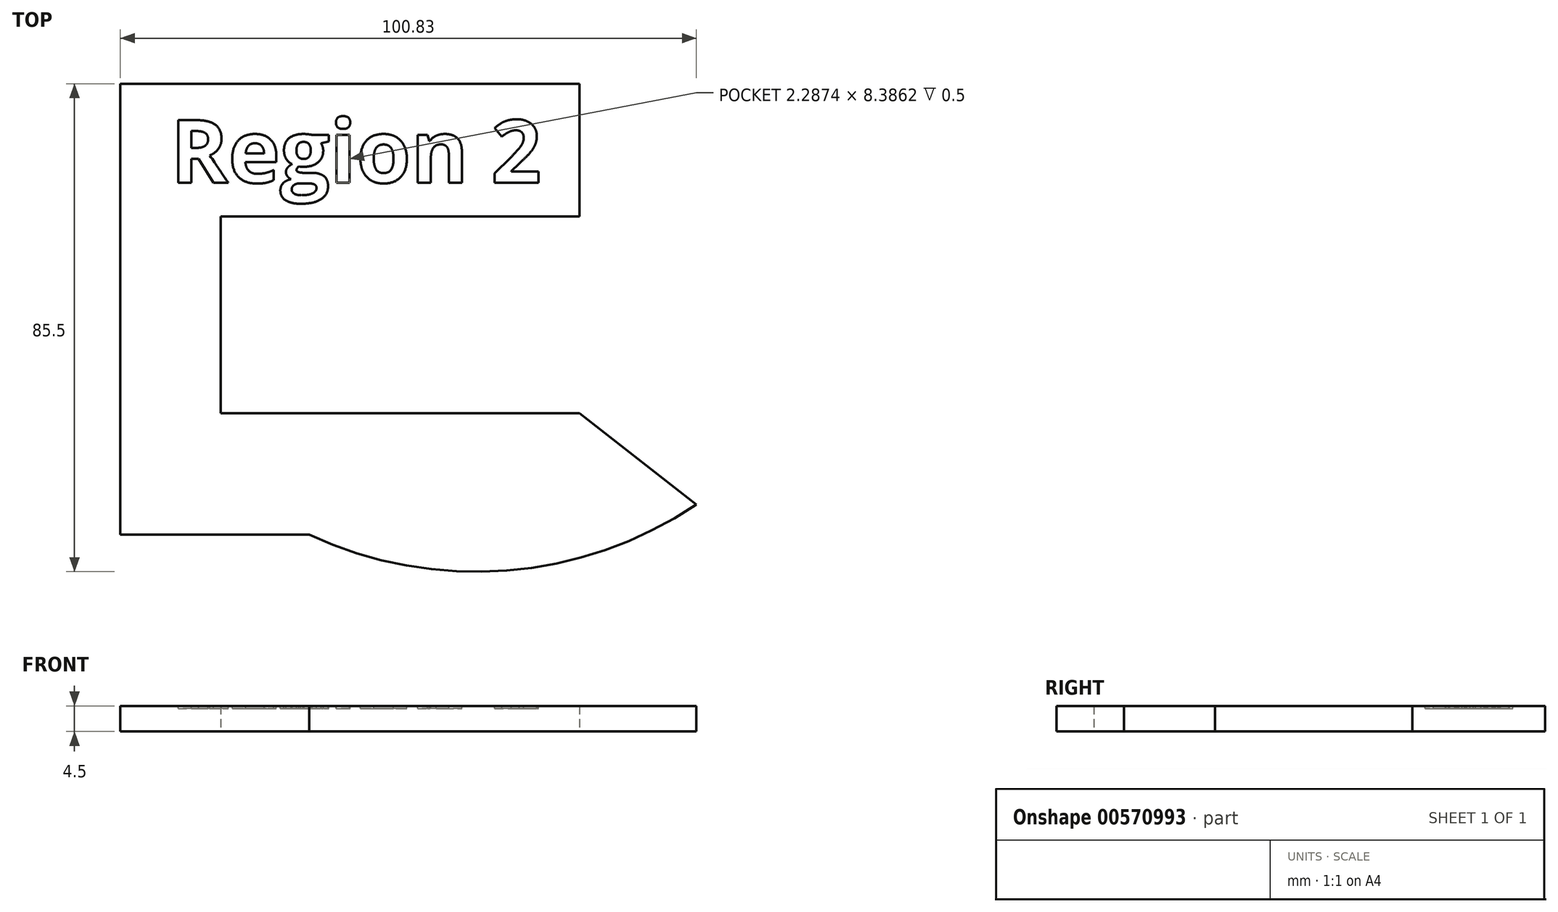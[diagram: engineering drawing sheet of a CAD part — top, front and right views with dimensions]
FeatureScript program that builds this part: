
annotation { "Feature Type Name" : "Feature", "Feature Type Description" : "" }
export const myFeature = defineFeature(function(context is Context, id is Id, definition is map)
    precondition{}
    {
        {
            var Q0;
            Q0=qCreatedBy(makeId("Top.planeOp"),FACE);
            var sketch = newSketch(context, id + "F0", { "sketchPlane" : qUnion([Q0])});
            skLineSegment(sketch, "E0.bottom", {"start": v(27.72, 0) * mm, "end": v(60.76, 0) * mm});
            skLineSegment(sketch, "E0.left", {"start": v(0, 0) * mm, "end": v(0, 99.58) * mm, "construction": true});
            skArc(sketch, "E1", {"start": v(60.76, 0) * mm, "mid": v(95.35, -6.3) * mm, "end": v(128.55, 5.27) * mm});
            skPoint(sketch, "E2.firstSnap0", {"position": v(0, 49.8) * mm});
            skLineSegment(sketch, "E2.top", {"start": v(50, 41) * mm, "end": v(130, 41) * mm, "construction": true});
            skLineSegment(sketch, "E3", {"start": v(90, 62.5) * mm, "end": v(90, 41) * mm});
            skLineSegment(sketch, "E4", {"start": v(27.72, 79) * mm, "end": v(108.08, 79) * mm});
            skLineSegment(sketch, "E5", {"start": v(108.08, 79) * mm, "end": v(108.08, 55.74) * mm});
            skLineSegment(sketch, "E6", {"start": v(108.08, 55.74) * mm, "end": v(45.3, 55.74) * mm});
            skLineSegment(sketch, "E7", {"start": v(45.3, 55.74) * mm, "end": v(45.3, 21.24) * mm});
            skLineSegment(sketch, "E8", {"start": v(45.3, 21.24) * mm, "end": v(108.08, 21.24) * mm});
            skLineSegment(sketch, "E9", {"start": v(108.08, 21.24) * mm, "end": v(128.55, 5.27) * mm});
            skLineSegment(sketch, "E10", {"start": v(27.72, 79) * mm, "end": v(27.72, 0) * mm});
            skSolve(sketch);
        }
        {
            var Q0;
            Q0 = qSketchRegion(id + "F0", true);
            extrude(context, id + "F1", {"entities" : qUnion([Q0]), "depth" : 4.5 * mm, "offsetDistance" : 25 * mm});
        }
        {
            var Q0;
            Q0=makeQuery(id+"F1.opExtrude","CAP_FACE",FACE,{"disambiguationData":[OSD([sQuery(id+"F0.wireOp",EDGE,"E0.bottom"),sQuery(id+"F0.wireOp",EDGE,"E1"),sQuery(id+"F0.wireOp",EDGE,"E4"),sQuery(id+"F0.wireOp",EDGE,"E5"),sQuery(id+"F0.wireOp",EDGE,"E6"),sQuery(id+"F0.wireOp",EDGE,"E7"),sQuery(id+"F0.wireOp",EDGE,"E8"),sQuery(id+"F0.wireOp",EDGE,"E9"),sQuery(id+"F0.wireOp",EDGE,"E10")])],"isStart":false});
            var sketch = newSketch(context, id + "F2", { "sketchPlane" : qUnion([Q0])});
            skText(sketch, "E11", { "text": "Region 2", "fontName": "OpenSans-Bold.ttf"});
            const initialGuessF2  = {"E11": [0.03648, 0.06167, 1, 0, 0.01106]};
            skSetInitialGuess(sketch, initialGuessF2);
            skSolve(sketch);
        }
        {
            var Q0;
            Q0 = qSketchRegion(id + "F2", true);
            extrude(context, id + "F3", {"entities" : qUnion([Q0]), "operationType" : NewBodyOperationType.REMOVE, "oppositeDirection" : true, "depth" : 0.5 * mm, "offsetDistance" : 25 * mm});
        }
    });
